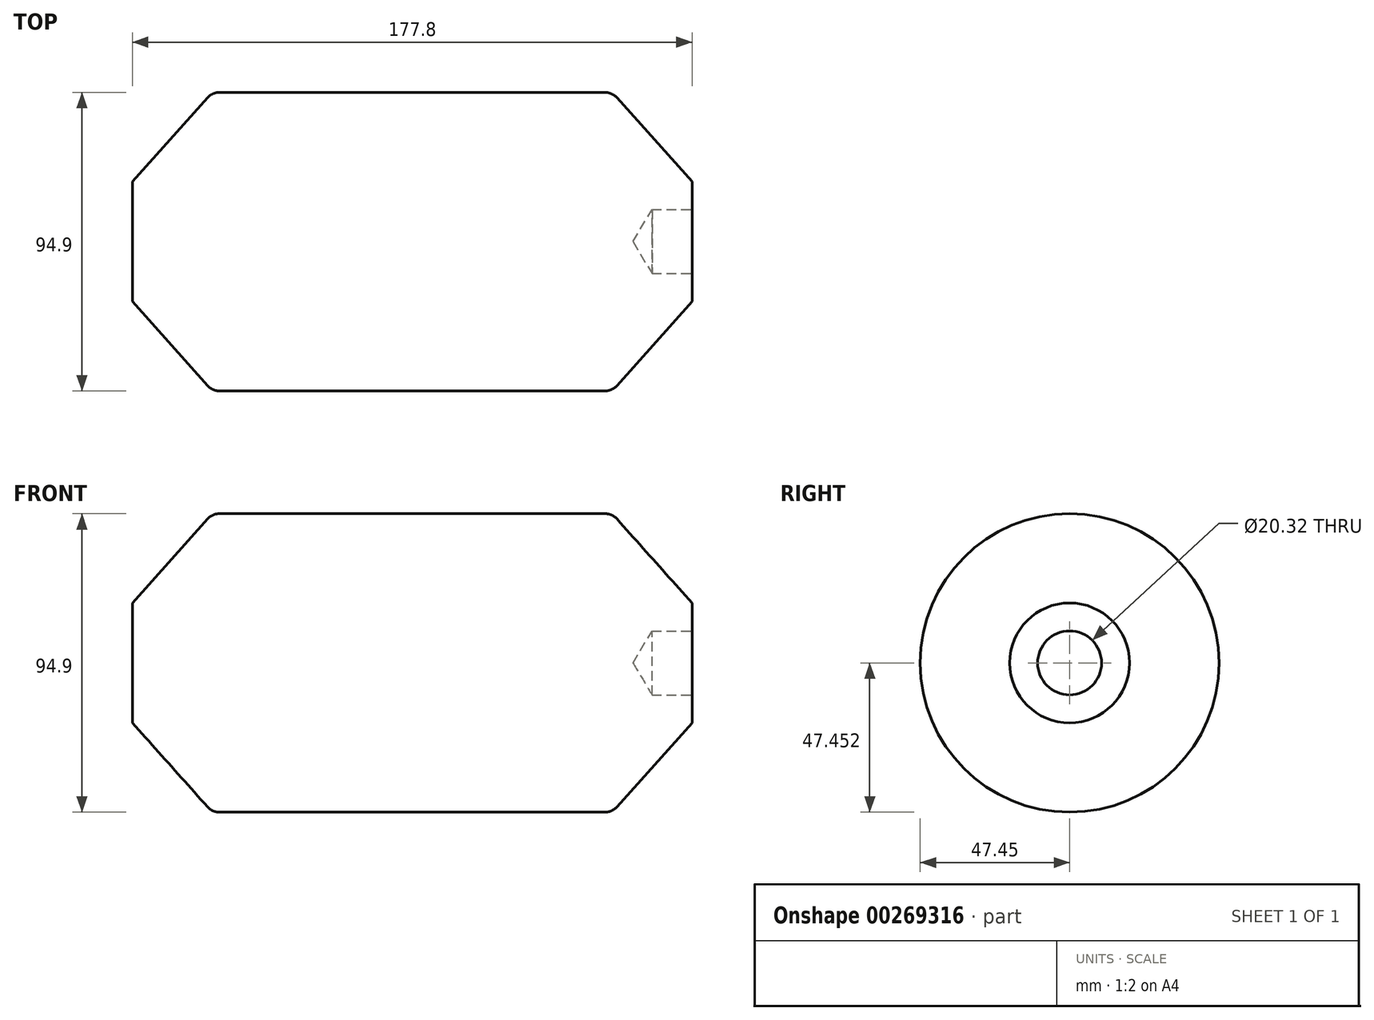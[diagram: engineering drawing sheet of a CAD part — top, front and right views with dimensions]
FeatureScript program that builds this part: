
annotation { "Feature Type Name" : "Feature", "Feature Type Description" : "" }
export const myFeature = defineFeature(function(context is Context, id is Id, definition is map)
    precondition{}
    {
        {
            var Q0;
            Q0=qCreatedBy(makeId("Front.planeOp"),FACE);
            var sketch = newSketch(context, id + "F0", { "sketchPlane" : qUnion([Q0])});
            skLineSegment(sketch, "E0", {"start": v(0, 0) * mm, "end": v(127, 0) * mm});
            skLineSegment(sketch, "E1", {"start": v(127, 0) * mm, "end": v(152.4, -28.4) * mm});
            skLineSegment(sketch, "E2", {"start": v(63.5, 0) * mm, "end": v(63.5, -28.4) * mm, "construction": true});
            skLineSegment(sketch, "E3.MirrorCS", {"start": v(0, 0) * mm, "end": v(-25.4, -28.4) * mm});
            skLineSegment(sketch, "E4", {"start": v(-25.4, -28.4) * mm, "end": v(-25.4, -47.45) * mm});
            skLineSegment(sketch, "E5.MirrorCS", {"start": v(152.4, -28.4) * mm, "end": v(152.4, -47.45) * mm});
            skLineSegment(sketch, "E6", {"start": v(-25.4, -47.45) * mm, "end": v(152.4, -47.45) * mm});
            skSolve(sketch);
        }
        {
            var Q0;
            Q0=makeQuery(id+"F0.imprint","IMPRINT",FACE,{"disambiguationData":[TD([[makeQuery(id+"F0.imprint","IMPRINT",EDGE,{"derivedFrom":sQuery(id+"F0.wireOp",EDGE,"E0")}),-1.0]])]});
            var Q1;
            Q1=sQuery(id+"F0.wireOp",EDGE,"E6");
            revolve(context, id + "F1", {"entities" : qUnion([Q0]), "axis" : qUnion([Q1]), "revolveType" : RevolveType.FULL});
        }
        {
            var Q0;
            Q0=makeQuery(id+"F1.opRevolve","SWEPT_FACE",FACE,{"disambiguationData":[OSD([sQuery(id+"F0.wireOp",EDGE,"E5.MirrorCS")])]});
            var sketch = newSketch(context, id + "F2", { "sketchPlane" : qUnion([Q0])});
            skCircle(sketch, "E7", {"center": v(0, -47.45) * mm, "radius": 10.74 * mm});
            skSolve(sketch);
        }
        {
            var Q0;
            Q0=sQuery(id+"F2.wireOp",VERTEX,"E7.center");
            var Q1;
            Q1=makeQuery(id+"F1.opRevolve","SWEPT_BODY",BODY,{"disambiguationData":[OSD([sQuery(id+"F0.wireOp",EDGE,"E0"),sQuery(id+"F0.wireOp",EDGE,"E1"),sQuery(id+"F0.wireOp",EDGE,"E3.MirrorCS"),sQuery(id+"F0.wireOp",EDGE,"E4"),sQuery(id+"F0.wireOp",EDGE,"E5.MirrorCS"),sQuery(id+"F0.wireOp",EDGE,"E6")])]});
            hole(context, id + "F4", {"style" : HoleStyle.SIMPLE, "endStyle" : HoleEndStyle.BLIND, "holeDiameter" : 20.32 * mm, "holeDepth" : 12.7 * mm, "tappedDepth" : 12.7 * mm, "tapClearance" : 3, "locations" : qUnion([Q0]), "scope" : qUnion([Q1])});
        }
        {
            var Q0;
            Q0=makeQuery(id+"F1.opRevolve","SWEPT_EDGE",EDGE,{"disambiguationData":[OSD([sQuery(id+"F0.wireOp",EDGE,"E0"),sQuery(id+"F0.wireOp",EDGE,"E1")])]});
            fillet(context, id + "F3", {"entities" : qUnion([Q0]), "radius" : 5.08 * mm, "tangentPropagation" : true, "allowEdgeOverflow" : false});
        }
        {
            var Q0;
            Q0=makeQuery(id+"F1.opRevolve","SWEPT_EDGE",EDGE,{"disambiguationData":[OSD([sQuery(id+"F0.wireOp",EDGE,"E0"),sQuery(id+"F0.wireOp",EDGE,"E3.MirrorCS")])]});
            fillet(context, id + "F5", {"entities" : qUnion([Q0]), "radius" : 5.08 * mm, "tangentPropagation" : true, "allowEdgeOverflow" : false});
        }
    });
